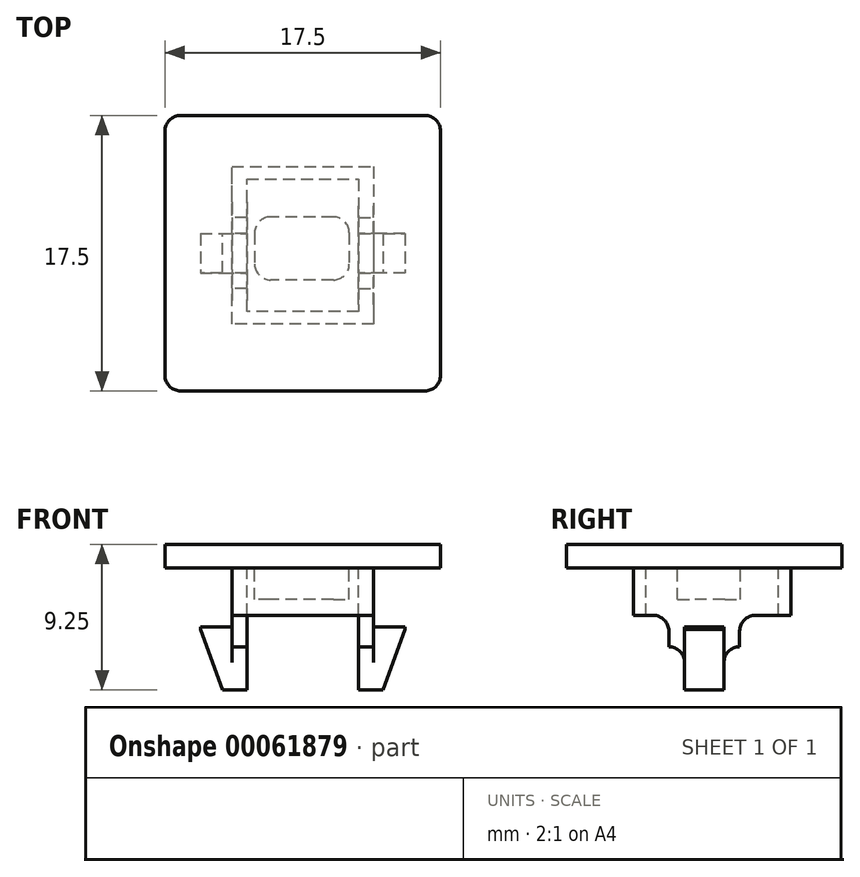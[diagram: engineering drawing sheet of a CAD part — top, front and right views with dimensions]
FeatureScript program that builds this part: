
annotation { "Feature Type Name" : "Feature", "Feature Type Description" : "" }
export const myFeature = defineFeature(function(context is Context, id is Id, definition is map)
    precondition{}
    {
        {
            var Q0;
            Q0=qCreatedBy(makeId("Top.planeOp"),FACE);
            var sketch = newSketch(context, id + "F14", { "sketchPlane" : qUnion([Q0])});
            skLineSegment(sketch, "E0.bottom", {"start": v(-7.75, 8.75) * mm, "end": v(7.75, 8.75) * mm});
            skLineSegment(sketch, "E0.top", {"start": v(-7.75, -8.75) * mm, "end": v(7.75, -8.75) * mm});
            skLineSegment(sketch, "E0.left", {"start": v(-8.75, 7.75) * mm, "end": v(-8.75, -7.75) * mm});
            skLineSegment(sketch, "E0.right", {"start": v(8.75, 7.75) * mm, "end": v(8.75, -7.75) * mm});
            skPoint(sketch, "E1.visualSharp", {"position": v(-8.75, 8.75) * mm});
            skArc(sketch, "E1.filletArc", {"start": v(-7.75, 8.75) * mm, "mid": v(-8.46, 8.46) * mm, "end": v(-8.75, 7.75) * mm});
            skPoint(sketch, "E2.visualSharp", {"position": v(8.75, 8.75) * mm});
            skArc(sketch, "E2.filletArc", {"start": v(8.75, 7.75) * mm, "mid": v(8.46, 8.46) * mm, "end": v(7.75, 8.75) * mm});
            skPoint(sketch, "E3.visualSharp", {"position": v(8.75, -8.75) * mm});
            skArc(sketch, "E3.filletArc", {"start": v(7.75, -8.75) * mm, "mid": v(8.46, -8.46) * mm, "end": v(8.75, -7.75) * mm});
            skPoint(sketch, "E4.visualSharp", {"position": v(-8.75, -8.75) * mm});
            skArc(sketch, "E4.filletArc", {"start": v(-8.75, -7.75) * mm, "mid": v(-8.46, -8.46) * mm, "end": v(-7.75, -8.75) * mm});
            skText(sketch, "E5", { "text": "P", "fontName": "OpenSans-Bold.ttf"});
            const initialGuessFFZrm2SAvl7R064F9_0  = {"E5": [-0.003, -0.0035, 1, 0, 0.007]};
            skSetInitialGuess(sketch, initialGuessFFZrm2SAvl7R064F9_0);
            skSolve(sketch);
        }
        {
            var Q0;
            Q0=makeQuery(id+"F14.imprint","IMPRINT",FACE,{"disambiguationData":[TD([[makeQuery(id+"F14.imprint","IMPRINT",EDGE,{"derivedFrom":sQuery(id+"F14.wireOp",EDGE,"E0.bottom")}),-1.0]])]});
            var Q1;
            Q1=makeQuery(id+"F14.imprint","IMPRINT",FACE,{"disambiguationData":[TD([[makeQuery(id+"F14.imprint","IMPRINT",EDGE,{"derivedFrom":sQuery(id+"F14.wireOp",EDGE,"E5.sketch_text.stroke-0")}),1.0]])]});
            extrude(context, id + "F0", {"entities" : qUnion([Q0, Q1]), "depth" : 1.5 * mm});
        }
        {
            var Q0;
            Q0=makeQuery(id+"F0.opExtrude","CAP_FACE",FACE,{"disambiguationData":[OSD([sQuery(id+"F14.wireOp",EDGE,"E0.bottom"),sQuery(id+"F14.wireOp",EDGE,"E0.top"),sQuery(id+"F14.wireOp",EDGE,"E0.left"),sQuery(id+"F14.wireOp",EDGE,"E0.right"),sQuery(id+"F14.wireOp",EDGE,"E1.filletArc"),sQuery(id+"F14.wireOp",EDGE,"E2.filletArc"),sQuery(id+"F14.wireOp",EDGE,"E3.filletArc"),sQuery(id+"F14.wireOp",EDGE,"E4.filletArc"),sQuery(id+"F14.wireOp",EDGE,"E5.sketch_text.stroke-7"),sQuery(id+"F14.wireOp",EDGE,"E5.sketch_text.stroke-8"),sQuery(id+"F14.wireOp",EDGE,"E5.sketch_text.stroke-9"),sQuery(id+"F14.wireOp",EDGE,"E5.sketch_text.stroke-10"),sQuery(id+"F14.wireOp",EDGE,"E5.sketch_text.stroke-11"),sQuery(id+"F14.wireOp",EDGE,"E5.sketch_text.stroke-12"),sQuery(id+"F14.wireOp",EDGE,"E5.sketch_text.stroke-13"),sQuery(id+"F14.wireOp",EDGE,"E5.sketch_text.stroke-14"),sQuery(id+"F14.wireOp",EDGE,"E5.sketch_text.stroke-15")])],"isStart":true});
            var sketch = newSketch(context, id + "F1", { "sketchPlane" : qUnion([Q0])});
            skLineSegment(sketch, "E6", {"start": v(3.55, -4.7) * mm, "end": v(3.55, 3.7) * mm});
            skLineSegment(sketch, "E7", {"start": v(3.55, 3.7) * mm, "end": v(-3.55, 3.7) * mm});
            skLineSegment(sketch, "E8", {"start": v(-3.55, 3.7) * mm, "end": v(-3.55, -4.7) * mm});
            skLineSegment(sketch, "E9", {"start": v(-3.55, -4.7) * mm, "end": v(3.55, -4.7) * mm});
            skLineSegment(sketch, "E10", {"start": v(4.5, -5.5) * mm, "end": v(4.5, 4.5) * mm});
            skLineSegment(sketch, "E11", {"start": v(4.5, 4.5) * mm, "end": v(-4.5, 4.5) * mm});
            skLineSegment(sketch, "E12", {"start": v(-4.5, 4.5) * mm, "end": v(-4.5, -5.5) * mm});
            skLineSegment(sketch, "E13", {"start": v(-4.5, -5.5) * mm, "end": v(4.5, -5.5) * mm});
            skSolve(sketch);
        }
        {
            var Q0;
            Q0=makeQuery(id+"F1.imprint","IMPRINT",FACE,{"disambiguationData":[TD([[makeQuery(id+"F1.imprint","IMPRINT",EDGE,{"derivedFrom":sQuery(id+"F1.wireOp",EDGE,"E6")}),-1.0]])]});
            extrude(context, id + "F2", {"entities" : qUnion([Q0]), "operationType" : NewBodyOperationType.ADD, "depth" : 5 * mm});
        }
        {
            var Q0;
            Q0=makeQuery(id+"F2.opExtrude","SWEPT_FACE",FACE,{"disambiguationData":[OSD([sQuery(id+"F1.wireOp",EDGE,"E10")])]});
            var sketch = newSketch(context, id + "F3", { "sketchPlane" : qUnion([Q0])});
            skLineSegment(sketch, "E14.bottom", {"start": v(1.25, -3.75) * mm, "end": v(-1.25, -3.75) * mm});
            skLineSegment(sketch, "E14.top", {"start": v(1.25, -7.75) * mm, "end": v(-1.25, -7.75) * mm});
            skLineSegment(sketch, "E14.left", {"start": v(1.25, -3.75) * mm, "end": v(1.25, -7.75) * mm});
            skLineSegment(sketch, "E14.right", {"start": v(-1.25, -3.75) * mm, "end": v(-1.25, -7.75) * mm});
            skSolve(sketch);
        }
        {
            var Q0;
            {var subQ0=sQuery(id+"F3.wireOp",EDGE,"E14.bottom");Q0=makeQuery(id+"F3.imprint","IMPRINT",FACE,{"disambiguationData":[TD([[makeQuery(id+"F3.imprint","IMPRINT",EDGE,{"derivedFrom":subQ0}),1.0]])]});}
            var Q1;
            {var subQ0=sQuery(id+"F3.wireOp",EDGE,"E14.top");Q1=makeQuery(id+"F3.imprint","IMPRINT",FACE,{"disambiguationData":[TD([[makeQuery(id+"F3.imprint","IMPRINT",EDGE,{"derivedFrom":subQ0}),-1.0]])]});}
            var Q2;
            Q2=makeQuery(id+"F2.opExtrude","SWEPT_FACE",FACE,{"disambiguationData":[OSD([sQuery(id+"F1.wireOp",EDGE,"E6")])]});
            extrude(context, id + "F4", {"entities" : qUnion([Q0, Q1]), "operationType" : NewBodyOperationType.ADD, "depth" : 2 * mm, "hasSecondDirection" : true, "secondDirectionBound" : SecondDirectionBoundingType.UP_TO_SURFACE, "secondDirectionOppositeDirection" : true, "secondDirectionBoundEntityFace" : qUnion([Q2]), "secondDirectionDepth" : 1 * mm});
        }
        {
            var Q0;
            Q0=makeQuery(id+"F4.opExtrude","CAP_EDGE",EDGE,{"disambiguationData":[OSD([sQuery(id+"F3.wireOp",EDGE,"E14.top")])],"isStart":false});
            chamfer(context, id + "F5", {"entities" : qUnion([Q0]), "chamferType" : ChamferType.OFFSET_ANGLE, "width" : 1.4 * mm, "oppositeDirection" : false, "angle" : 70 * degree, "tangentPropagation" : true});
        }
        {
            var Q0;
            Q0 = qSketchRegion(id + "F3", true);
            extrude(context, id + "F6", {"entities" : qUnion([Q0]), "operationType" : NewBodyOperationType.ADD, "oppositeDirection" : true, "depth" : 11 * mm, "hasSecondDirection" : true, "secondDirectionOppositeDirection" : true, "secondDirectionDepth" : 8.05 * mm});
        }
        {
            var Q0;
            Q0=makeQuery(id+"F6.opExtrude","CAP_EDGE",EDGE,{"disambiguationData":[OSD([sQuery(id+"F3.wireOp",EDGE,"E14.top")])],"isStart":false});
            chamfer(context, id + "F7", {"entities" : qUnion([Q0]), "chamferType" : ChamferType.OFFSET_ANGLE, "width" : 1.4 * mm, "oppositeDirection" : true, "angle" : 70 * degree, "tangentPropagation" : true});
        }
        {
            var Q0;
            Q0=makeQuery(id+"F6.boolean.opBoolean","INTERSECT",EDGE,{"derivedFrom":[makeQuery(id+"F2.opExtrude","CAP_FACE",FACE,{"disambiguationData":[OSD([sQuery(id+"F1.wireOp",EDGE,"E6"),sQuery(id+"F1.wireOp",EDGE,"E7"),sQuery(id+"F1.wireOp",EDGE,"E8"),sQuery(id+"F1.wireOp",EDGE,"E9"),sQuery(id+"F1.wireOp",EDGE,"E10"),sQuery(id+"F1.wireOp",EDGE,"E11"),sQuery(id+"F1.wireOp",EDGE,"E12"),sQuery(id+"F1.wireOp",EDGE,"E13")])],"isStart":false}),makeQuery(id+"F6.opExtrude","SWEPT_FACE",FACE,{"disambiguationData":[OSD([sQuery(id+"F3.wireOp",EDGE,"E14.right")])]})]});
            var Q1;
            Q1=makeQuery(id+"F6.boolean.opBoolean","INTERSECT",EDGE,{"derivedFrom":[makeQuery(id+"F2.opExtrude","CAP_FACE",FACE,{"disambiguationData":[OSD([sQuery(id+"F1.wireOp",EDGE,"E6"),sQuery(id+"F1.wireOp",EDGE,"E7"),sQuery(id+"F1.wireOp",EDGE,"E8"),sQuery(id+"F1.wireOp",EDGE,"E9"),sQuery(id+"F1.wireOp",EDGE,"E10"),sQuery(id+"F1.wireOp",EDGE,"E11"),sQuery(id+"F1.wireOp",EDGE,"E12"),sQuery(id+"F1.wireOp",EDGE,"E13")])],"isStart":false}),makeQuery(id+"F6.opExtrude","SWEPT_FACE",FACE,{"disambiguationData":[OSD([sQuery(id+"F3.wireOp",EDGE,"E14.left")])]})]});
            var Q2;
            Q2=makeQuery(id+"F4.boolean.opBoolean","INTERSECT",EDGE,{"derivedFrom":[makeQuery(id+"F2.opExtrude","CAP_FACE",FACE,{"disambiguationData":[OSD([sQuery(id+"F1.wireOp",EDGE,"E6"),sQuery(id+"F1.wireOp",EDGE,"E7"),sQuery(id+"F1.wireOp",EDGE,"E8"),sQuery(id+"F1.wireOp",EDGE,"E9"),sQuery(id+"F1.wireOp",EDGE,"E10"),sQuery(id+"F1.wireOp",EDGE,"E11"),sQuery(id+"F1.wireOp",EDGE,"E12"),sQuery(id+"F1.wireOp",EDGE,"E13")])],"isStart":false}),makeQuery(id+"F4.opExtrude","SWEPT_FACE",FACE,{"disambiguationData":[OSD([sQuery(id+"F3.wireOp",EDGE,"E14.right")])]})]});
            var Q3;
            Q3=makeQuery(id+"F4.boolean.opBoolean","INTERSECT",EDGE,{"derivedFrom":[makeQuery(id+"F2.opExtrude","CAP_FACE",FACE,{"disambiguationData":[OSD([sQuery(id+"F1.wireOp",EDGE,"E6"),sQuery(id+"F1.wireOp",EDGE,"E7"),sQuery(id+"F1.wireOp",EDGE,"E8"),sQuery(id+"F1.wireOp",EDGE,"E9"),sQuery(id+"F1.wireOp",EDGE,"E10"),sQuery(id+"F1.wireOp",EDGE,"E11"),sQuery(id+"F1.wireOp",EDGE,"E12"),sQuery(id+"F1.wireOp",EDGE,"E13")])],"isStart":false}),makeQuery(id+"F4.opExtrude","SWEPT_FACE",FACE,{"disambiguationData":[OSD([sQuery(id+"F3.wireOp",EDGE,"E14.left")])]})]});
            fillet(context, id + "F8", {"entities" : qUnion([Q0, Q1, Q2, Q3]), "radius" : 1 * mm, "tangentPropagation" : true, "allowEdgeOverflow" : false});
        }
        {
            var Q0;
            Q0=makeQuery(id+"F14.imprint","IMPRINT",FACE,{"disambiguationData":[TD([[makeQuery(id+"F14.imprint","IMPRINT",EDGE,{"derivedFrom":sQuery(id+"F14.wireOp",EDGE,"E5.sketch_text.stroke-0")}),-1.0]])]});
            var Q1;
            Q1=makeQuery(id+"F0.opExtrude","CAP_FACE",FACE,{"disambiguationData":[OSD([sQuery(id+"F14.wireOp",EDGE,"E0.bottom"),sQuery(id+"F14.wireOp",EDGE,"E0.top"),sQuery(id+"F14.wireOp",EDGE,"E0.left"),sQuery(id+"F14.wireOp",EDGE,"E0.right"),sQuery(id+"F14.wireOp",EDGE,"E1.filletArc"),sQuery(id+"F14.wireOp",EDGE,"E2.filletArc"),sQuery(id+"F14.wireOp",EDGE,"E3.filletArc"),sQuery(id+"F14.wireOp",EDGE,"E4.filletArc"),sQuery(id+"F14.wireOp",EDGE,"E5.sketch_text.stroke-7"),sQuery(id+"F14.wireOp",EDGE,"E5.sketch_text.stroke-8"),sQuery(id+"F14.wireOp",EDGE,"E5.sketch_text.stroke-9"),sQuery(id+"F14.wireOp",EDGE,"E5.sketch_text.stroke-10"),sQuery(id+"F14.wireOp",EDGE,"E5.sketch_text.stroke-11"),sQuery(id+"F14.wireOp",EDGE,"E5.sketch_text.stroke-12"),sQuery(id+"F14.wireOp",EDGE,"E5.sketch_text.stroke-13"),sQuery(id+"F14.wireOp",EDGE,"E5.sketch_text.stroke-14"),sQuery(id+"F14.wireOp",EDGE,"E5.sketch_text.stroke-15")])],"isStart":false});
            extrude(context, id + "F9", {"entities" : qUnion([Q0]), "endBound" : BoundingType.UP_TO_SURFACE, "endBoundEntityFace" : qUnion([Q1]), "depth" : 25 * mm});
        }
        {
            var Q0;
            {var subQ0=sQuery(id+"F14.wireOp",EDGE,"E5.sketch_text.stroke-15");var subQ1=sQuery(id+"F14.wireOp",EDGE,"E5.sketch_text.stroke-13");var subQ2=sQuery(id+"F14.wireOp",EDGE,"E5.sketch_text.stroke-14");var subQ3=sQuery(id+"F14.wireOp",EDGE,"E5.sketch_text.stroke-12");var subQ4=sQuery(id+"F14.wireOp",EDGE,"E5.sketch_text.stroke-11");var subQ5=sQuery(id+"F14.wireOp",EDGE,"E5.sketch_text.stroke-8");var subQ6=sQuery(id+"F14.wireOp",EDGE,"E5.sketch_text.stroke-7");var subQ7=sQuery(id+"F14.wireOp",EDGE,"E5.sketch_text.stroke-9");var subQ8=sQuery(id+"F14.wireOp",EDGE,"E5.sketch_text.stroke-10");Q0=makeQuery(id+"F2.boolean.opBoolean","SPLIT",FACE,{"disambiguationData":[TD([makeQuery(id+"F0.opExtrude","SWEPT_FACE",FACE,{"disambiguationData":[OSD([subQ6])]})])],"derivedFrom":makeQuery(id+"F0.opExtrude","CAP_FACE",FACE,{"disambiguationData":[OSD([sQuery(id+"F14.wireOp",EDGE,"E0.bottom"),sQuery(id+"F14.wireOp",EDGE,"E0.top"),sQuery(id+"F14.wireOp",EDGE,"E0.left"),sQuery(id+"F14.wireOp",EDGE,"E0.right"),sQuery(id+"F14.wireOp",EDGE,"E1.filletArc"),sQuery(id+"F14.wireOp",EDGE,"E2.filletArc"),sQuery(id+"F14.wireOp",EDGE,"E3.filletArc"),sQuery(id+"F14.wireOp",EDGE,"E4.filletArc"),subQ6,subQ5,subQ7,subQ8,subQ4,subQ3,subQ1,subQ2,subQ0])],"isStart":true})});}
            var sketch = newSketch(context, id + "F10", { "sketchPlane" : qUnion([Q0])});
            skLineSegment(sketch, "E15.bottom", {"start": v(1.95, -2.3) * mm, "end": v(-2.05, -2.3) * mm});
            skLineSegment(sketch, "E15.top", {"start": v(1.95, 1.7) * mm, "end": v(-2.05, 1.7) * mm});
            skLineSegment(sketch, "E15.left", {"start": v(2.95, -1.3) * mm, "end": v(2.95, 0.7) * mm});
            skLineSegment(sketch, "E15.right", {"start": v(-3.05, -1.3) * mm, "end": v(-3.05, 0.7) * mm});
            skPoint(sketch, "E16.visualSharp", {"position": v(2.95, -2.3) * mm});
            skArc(sketch, "E16.filletArc", {"start": v(1.95, -2.3) * mm, "mid": v(2.66, -2) * mm, "end": v(2.95, -1.3) * mm});
            skPoint(sketch, "E17.visualSharp", {"position": v(-3.05, -2.3) * mm});
            skArc(sketch, "E17.filletArc", {"start": v(-3.05, -1.3) * mm, "mid": v(-2.76, -2) * mm, "end": v(-2.05, -2.3) * mm});
            skPoint(sketch, "E18.visualSharp", {"position": v(-3.05, 1.7) * mm});
            skArc(sketch, "E18.filletArc", {"start": v(-2.05, 1.7) * mm, "mid": v(-2.76, 1.4) * mm, "end": v(-3.05, 0.7) * mm});
            skPoint(sketch, "E19.visualSharp", {"position": v(2.95, 1.7) * mm});
            skArc(sketch, "E19.filletArc", {"start": v(2.95, 0.7) * mm, "mid": v(2.66, 1.4) * mm, "end": v(1.95, 1.7) * mm});
            skSolve(sketch);
        }
        {
            var Q0;
            Q0=makeQuery(id+"F10.imprint","IMPRINT",FACE,{"disambiguationData":[TD([[makeQuery(id+"F10.imprint","IMPRINT",EDGE,{"derivedFrom":sQuery(id+"F10.wireOp",EDGE,"E15.left")}),1.0]])]});
            var Q1;
            {var subQ0=sQuery(id+"F10.wireOp",EDGE,"E15.right");Q1=makeQuery(id+"F10.imprint","IMPRINT",FACE,{"disambiguationData":[TD([[makeQuery(id+"F10.imprint","IMPRINT",EDGE,{"derivedFrom":subQ0}),-1.0]])]});}
            var Q2;
            Q2=makeQuery(id+"F10.imprint","IMPRINT",FACE,{"disambiguationData":[TD([[makeQuery(id+"F10.imprint","IMPRINT",EDGE,{"derivedFrom":makeQuery(id+"F0.opExtrude","CAP_EDGE",EDGE,{"disambiguationData":[OSD([sQuery(id+"F14.wireOp",EDGE,"E5.sketch_text.stroke-7")])],"isStart":true})}),1.0]])]});
            extrude(context, id + "F11", {"entities" : qUnion([Q0, Q1, Q2]), "operationType" : NewBodyOperationType.ADD, "depth" : 2 * mm});
        }
        {
            var Q0;
            {var subQ0=sQuery(id+"F1.wireOp",EDGE,"E10");var subQ1=sQuery(id+"F1.wireOp",EDGE,"E9");var subQ6=sQuery(id+"F1.wireOp",EDGE,"E8");var subQ7=sQuery(id+"F1.wireOp",EDGE,"E6");var subQ8=sQuery(id+"F1.wireOp",EDGE,"E12");var subQ9=sQuery(id+"F1.wireOp",EDGE,"E13");Q0=makeQuery(id+"F6.boolean.opBoolean","SPLIT",FACE,{"disambiguationData":[TD([makeQuery(id+"F2.opExtrude","SWEPT_FACE",FACE,{"disambiguationData":[OSD([subQ1])]})])],"derivedFrom":makeQuery(id+"F2.opExtrude","CAP_FACE",FACE,{"disambiguationData":[OSD([subQ7,sQuery(id+"F1.wireOp",EDGE,"E7"),subQ6,subQ1,subQ0,sQuery(id+"F1.wireOp",EDGE,"E11"),subQ8,subQ9])],"isStart":false})});}
            var Q1;
            {var subQ0=sQuery(id+"F1.wireOp",EDGE,"E10");var subQ1=sQuery(id+"F1.wireOp",EDGE,"E8");var subQ6=sQuery(id+"F1.wireOp",EDGE,"E7");var subQ7=sQuery(id+"F1.wireOp",EDGE,"E6");var subQ8=sQuery(id+"F1.wireOp",EDGE,"E11");var subQ9=sQuery(id+"F1.wireOp",EDGE,"E12");Q1=makeQuery(id+"F6.boolean.opBoolean","SPLIT",FACE,{"disambiguationData":[TD([makeQuery(id+"F2.opExtrude","SWEPT_FACE",FACE,{"disambiguationData":[OSD([subQ6])]})])],"derivedFrom":makeQuery(id+"F2.opExtrude","CAP_FACE",FACE,{"disambiguationData":[OSD([subQ7,subQ6,subQ1,sQuery(id+"F1.wireOp",EDGE,"E9"),subQ0,subQ8,subQ9,sQuery(id+"F1.wireOp",EDGE,"E13")])],"isStart":false})});}
            extrude(context, id + "F12", {"entities" : qUnion([Q0, Q1]), "operationType" : NewBodyOperationType.REMOVE, "oppositeDirection" : true, "depth" : 2 * mm});
        }
        {
            var Q0;
            {var subQ0=sQuery(id+"F1.wireOp",EDGE,"E10");var subQ1=sQuery(id+"F1.wireOp",EDGE,"E9");var subQ3=sQuery(id+"F3.wireOp",EDGE,"E14.left");var subQ6=sQuery(id+"F1.wireOp",EDGE,"E8");var subQ7=sQuery(id+"F1.wireOp",EDGE,"E6");var subQ8=sQuery(id+"F1.wireOp",EDGE,"E12");var subQ9=sQuery(id+"F1.wireOp",EDGE,"E13");var subQ10=makeQuery(id+"F6.opExtrude","SWEPT_FACE",FACE,{"disambiguationData":[OSD([subQ3])]});var subQ11=sQuery(id+"F1.wireOp",EDGE,"E11");var subQ12=sQuery(id+"F1.wireOp",EDGE,"E7");var subQ13=makeQuery(id+"F2.opExtrude","CAP_FACE",FACE,{"disambiguationData":[OSD([subQ7,subQ12,subQ6,subQ1,subQ0,subQ11,subQ8,subQ9])],"isStart":false});Q0=makeQuery(id+"F12.boolean.opBoolean","COPY",EDGE,{"derivedFrom":makeQuery(id+"F12.opExtrude","CAP_EDGE",EDGE,{"disambiguationData":[OSD([subQ7,subQ12,subQ6,subQ1,subQ0,subQ11,subQ8,subQ9,subQ3]),TDD([makeQuery(id+"F8.opFillet","BLEND_EDGE",EDGE,{"blendedFrom":[makeQuery(id+"F6.boolean.opBoolean","INTERSECT",EDGE,{"derivedFrom":[subQ13,subQ10]}),makeQuery(id+"F6.boolean.opBoolean","SPLIT",FACE,{"disambiguationData":[TD([makeQuery(id+"F2.opExtrude","SWEPT_FACE",FACE,{"disambiguationData":[OSD([subQ1])]})])],"derivedFrom":subQ13})],"blendedInto":[makeQuery(id+"F6.boolean.opBoolean","SPLIT",FACE,{"disambiguationData":[TD([makeQuery(id+"F2.opExtrude","SWEPT_FACE",FACE,{"disambiguationData":[OSD([subQ1])]})])],"derivedFrom":subQ13})]})])],"isStart":false})});}
            var Q1;
            {var subQ0=sQuery(id+"F1.wireOp",EDGE,"E10");var subQ1=sQuery(id+"F1.wireOp",EDGE,"E9");var subQ2=sQuery(id+"F3.wireOp",EDGE,"E14.left");var subQ3=sQuery(id+"F1.wireOp",EDGE,"E8");var subQ4=sQuery(id+"F1.wireOp",EDGE,"E6");var subQ5=makeQuery(id+"F4.opExtrude","SWEPT_FACE",FACE,{"disambiguationData":[OSD([subQ2])]});var subQ6=sQuery(id+"F1.wireOp",EDGE,"E12");var subQ7=sQuery(id+"F1.wireOp",EDGE,"E13");var subQ8=sQuery(id+"F1.wireOp",EDGE,"E11");var subQ9=sQuery(id+"F1.wireOp",EDGE,"E7");var subQ10=makeQuery(id+"F2.opExtrude","CAP_FACE",FACE,{"disambiguationData":[OSD([subQ4,subQ9,subQ3,subQ1,subQ0,subQ8,subQ6,subQ7])],"isStart":false});Q1=makeQuery(id+"F12.boolean.opBoolean","COPY",EDGE,{"derivedFrom":makeQuery(id+"F12.opExtrude","CAP_EDGE",EDGE,{"disambiguationData":[OSD([subQ4,subQ9,subQ3,subQ1,subQ0,subQ8,subQ6,subQ7,subQ2]),TDD([makeQuery(id+"F8.opFillet","BLEND_EDGE",EDGE,{"blendedFrom":[makeQuery(id+"F4.boolean.opBoolean","INTERSECT",EDGE,{"derivedFrom":[subQ10,subQ5]}),makeQuery(id+"F6.boolean.opBoolean","SPLIT",FACE,{"disambiguationData":[TD([makeQuery(id+"F2.opExtrude","SWEPT_FACE",FACE,{"disambiguationData":[OSD([subQ1])]})])],"derivedFrom":subQ10})],"blendedInto":[makeQuery(id+"F6.boolean.opBoolean","SPLIT",FACE,{"disambiguationData":[TD([makeQuery(id+"F2.opExtrude","SWEPT_FACE",FACE,{"disambiguationData":[OSD([subQ1])]})])],"derivedFrom":subQ10})]})])],"isStart":false})});}
            var Q2;
            {var subQ0=sQuery(id+"F1.wireOp",EDGE,"E10");var subQ1=sQuery(id+"F1.wireOp",EDGE,"E8");var subQ2=sQuery(id+"F3.wireOp",EDGE,"E14.right");var subQ6=sQuery(id+"F1.wireOp",EDGE,"E7");var subQ7=sQuery(id+"F1.wireOp",EDGE,"E6");var subQ8=sQuery(id+"F1.wireOp",EDGE,"E11");var subQ9=sQuery(id+"F1.wireOp",EDGE,"E12");var subQ10=makeQuery(id+"F6.opExtrude","SWEPT_FACE",FACE,{"disambiguationData":[OSD([subQ2])]});var subQ11=sQuery(id+"F1.wireOp",EDGE,"E13");var subQ12=sQuery(id+"F1.wireOp",EDGE,"E9");var subQ13=makeQuery(id+"F2.opExtrude","CAP_FACE",FACE,{"disambiguationData":[OSD([subQ7,subQ6,subQ1,subQ12,subQ0,subQ8,subQ9,subQ11])],"isStart":false});Q2=makeQuery(id+"F12.boolean.opBoolean","COPY",EDGE,{"derivedFrom":makeQuery(id+"F12.opExtrude","CAP_EDGE",EDGE,{"disambiguationData":[OSD([subQ7,subQ6,subQ1,subQ12,subQ0,subQ8,subQ9,subQ11,subQ2]),TDD([makeQuery(id+"F8.opFillet","BLEND_EDGE",EDGE,{"blendedFrom":[makeQuery(id+"F6.boolean.opBoolean","INTERSECT",EDGE,{"derivedFrom":[subQ13,subQ10]}),makeQuery(id+"F6.boolean.opBoolean","SPLIT",FACE,{"disambiguationData":[TD([makeQuery(id+"F2.opExtrude","SWEPT_FACE",FACE,{"disambiguationData":[OSD([subQ6])]})])],"derivedFrom":subQ13})],"blendedInto":[makeQuery(id+"F6.boolean.opBoolean","SPLIT",FACE,{"disambiguationData":[TD([makeQuery(id+"F2.opExtrude","SWEPT_FACE",FACE,{"disambiguationData":[OSD([subQ6])]})])],"derivedFrom":subQ13})]})])],"isStart":false})});}
            var Q3;
            {var subQ0=sQuery(id+"F1.wireOp",EDGE,"E10");var subQ1=sQuery(id+"F1.wireOp",EDGE,"E8");var subQ2=sQuery(id+"F1.wireOp",EDGE,"E7");var subQ3=sQuery(id+"F1.wireOp",EDGE,"E6");var subQ4=sQuery(id+"F1.wireOp",EDGE,"E11");var subQ5=sQuery(id+"F1.wireOp",EDGE,"E12");var subQ6=sQuery(id+"F3.wireOp",EDGE,"E14.right");var subQ7=makeQuery(id+"F4.opExtrude","SWEPT_FACE",FACE,{"disambiguationData":[OSD([subQ6])]});var subQ8=sQuery(id+"F1.wireOp",EDGE,"E13");var subQ9=sQuery(id+"F1.wireOp",EDGE,"E9");var subQ10=makeQuery(id+"F2.opExtrude","CAP_FACE",FACE,{"disambiguationData":[OSD([subQ3,subQ2,subQ1,subQ9,subQ0,subQ4,subQ5,subQ8])],"isStart":false});Q3=makeQuery(id+"F12.boolean.opBoolean","COPY",EDGE,{"derivedFrom":makeQuery(id+"F12.opExtrude","CAP_EDGE",EDGE,{"disambiguationData":[OSD([subQ3,subQ2,subQ1,subQ9,subQ0,subQ4,subQ5,subQ8,subQ6]),TDD([makeQuery(id+"F8.opFillet","BLEND_EDGE",EDGE,{"blendedFrom":[makeQuery(id+"F4.boolean.opBoolean","INTERSECT",EDGE,{"derivedFrom":[subQ10,subQ7]}),makeQuery(id+"F6.boolean.opBoolean","SPLIT",FACE,{"disambiguationData":[TD([makeQuery(id+"F2.opExtrude","SWEPT_FACE",FACE,{"disambiguationData":[OSD([subQ2])]})])],"derivedFrom":subQ10})],"blendedInto":[makeQuery(id+"F6.boolean.opBoolean","SPLIT",FACE,{"disambiguationData":[TD([makeQuery(id+"F2.opExtrude","SWEPT_FACE",FACE,{"disambiguationData":[OSD([subQ2])]})])],"derivedFrom":subQ10})]})])],"isStart":false})});}
            fillet(context, id + "F13", {"entities" : qUnion([Q0, Q1, Q2, Q3]), "radius" : 1 * mm, "tangentPropagation" : true, "allowEdgeOverflow" : false});
        }
    });
